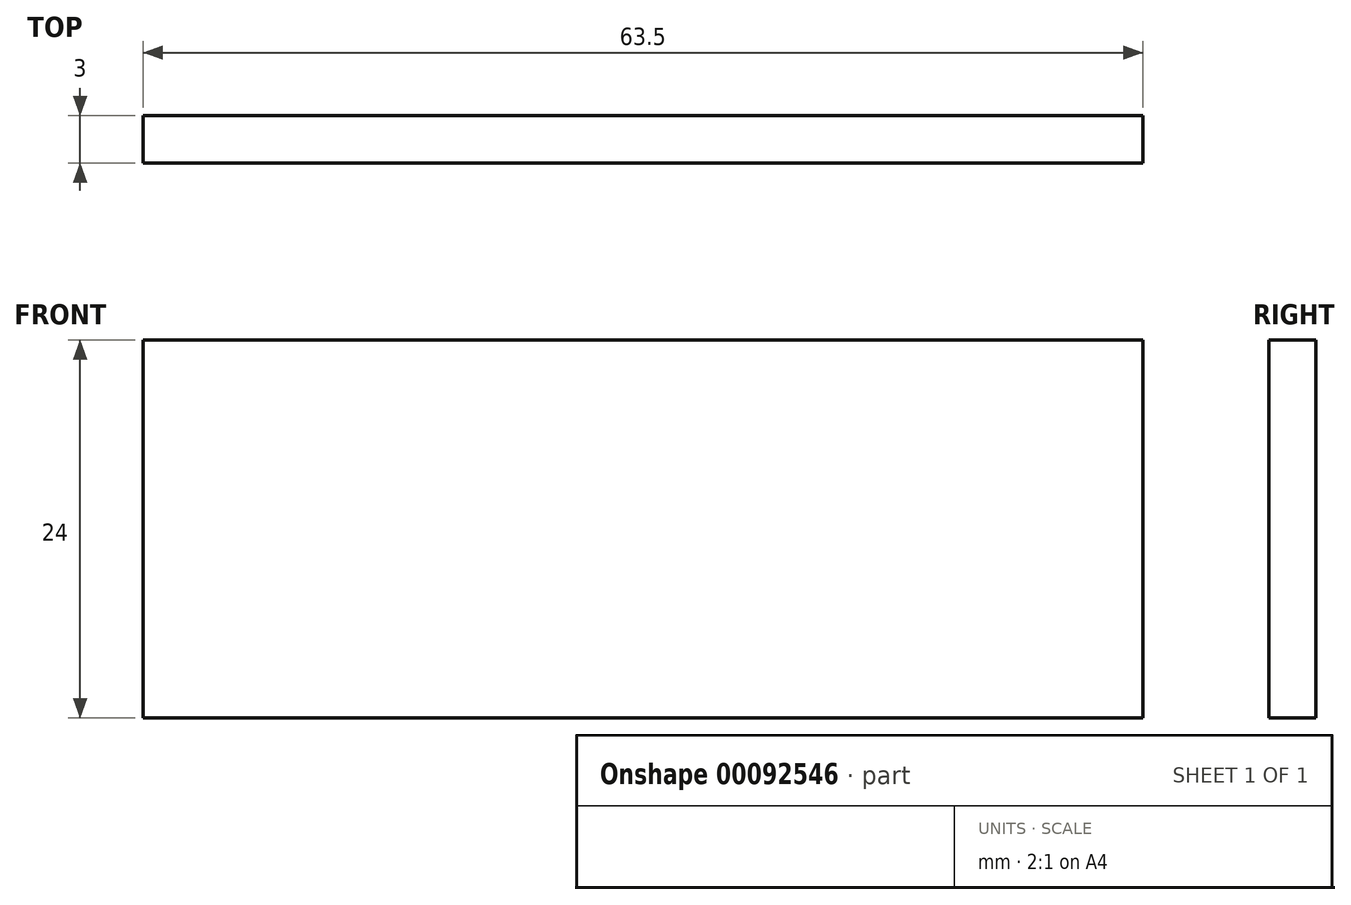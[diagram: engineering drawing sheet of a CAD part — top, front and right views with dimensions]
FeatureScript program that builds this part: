
annotation { "Feature Type Name" : "Feature", "Feature Type Description" : "" }
export const myFeature = defineFeature(function(context is Context, id is Id, definition is map)
    precondition{}
    {
        {
            var Q0;
            Q0=qCreatedBy(makeId("Front.planeOp"),FACE);
            var sketch = newSketch(context, id + "F0", { "sketchPlane" : qUnion([Q0])});
            skLineSegment(sketch, "E0.bottom", {"start": v(-32.92, 30.11) * mm, "end": v(30.58, 30.11) * mm});
            skLineSegment(sketch, "E0.top", {"start": v(-32.92, 6.11) * mm, "end": v(30.58, 6.11) * mm});
            skLineSegment(sketch, "E0.left", {"start": v(-32.92, 30.11) * mm, "end": v(-32.92, 6.11) * mm});
            skLineSegment(sketch, "E0.right", {"start": v(30.58, 30.11) * mm, "end": v(30.58, 6.11) * mm});
            skSolve(sketch);
        }
        {
            var Q0;
            Q0 = qSketchRegion(id + "F0", true);
            extrude(context, id + "F1", {"entities" : qUnion([Q0]), "depth" : 3 * mm});
        }
    });
